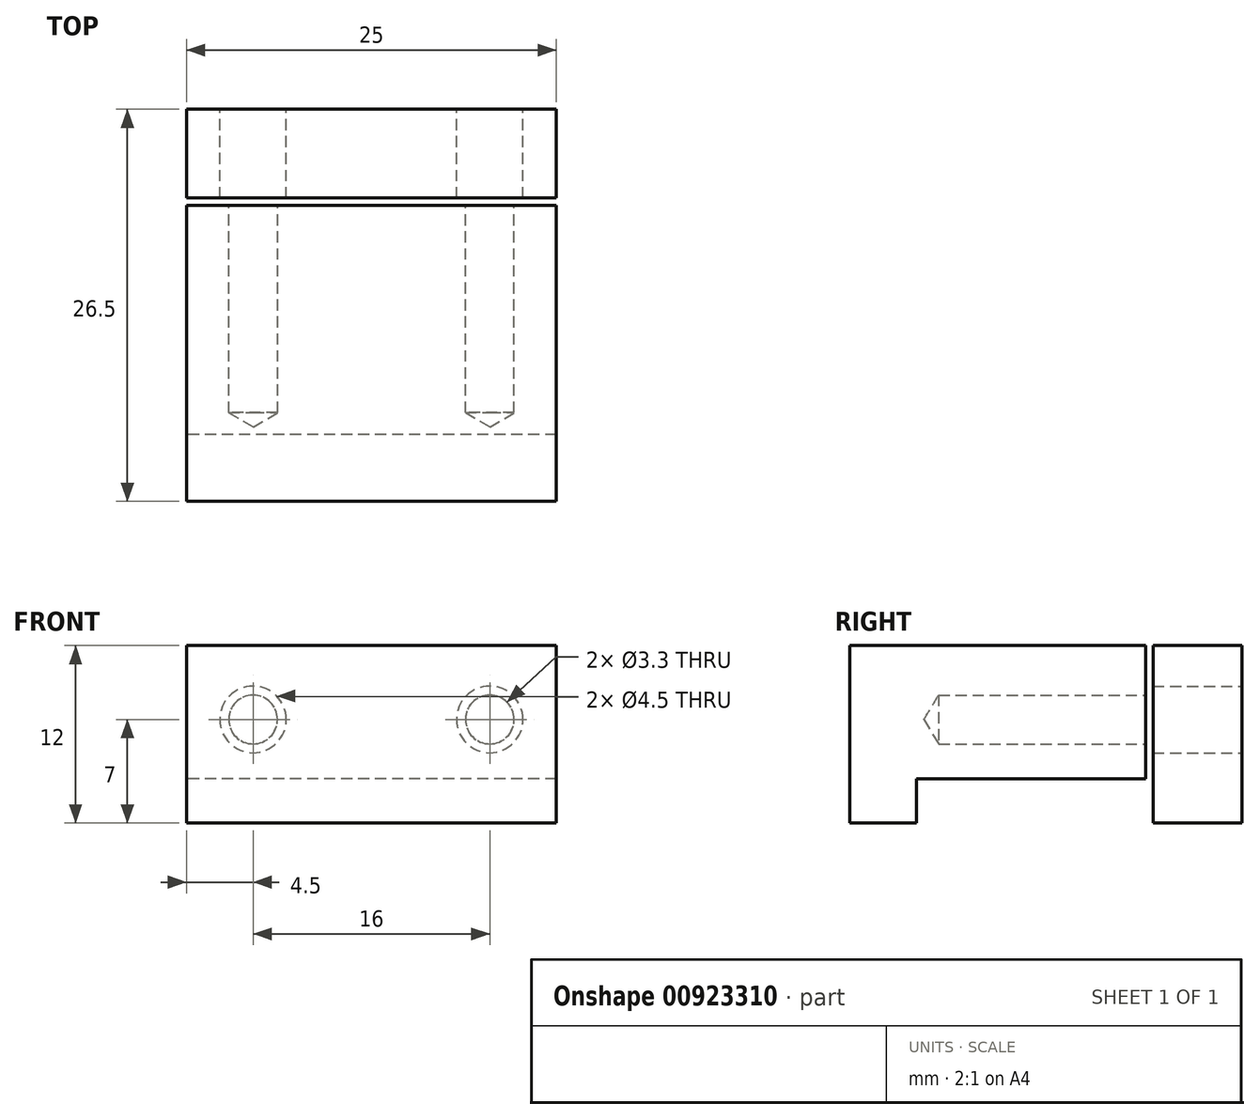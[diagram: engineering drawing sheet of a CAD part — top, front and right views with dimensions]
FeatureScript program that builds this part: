
annotation { "Feature Type Name" : "Feature", "Feature Type Description" : "" }
export const myFeature = defineFeature(function(context is Context, id is Id, definition is map)
    precondition{}
    {
        {
            var Q0;
            Q0=qCreatedBy(makeId("Front.planeOp"),FACE);
            var sketch = newSketch(context, id + "F0", { "sketchPlane" : qUnion([Q0])});
            skLineSegment(sketch, "E0.bottom", {"start": v(12.5, 6) * mm, "end": v(-12.5, 6) * mm});
            skLineSegment(sketch, "E0.top", {"start": v(12.5, -6) * mm, "end": v(-12.5, -6) * mm});
            skLineSegment(sketch, "E0.left", {"start": v(12.5, 6) * mm, "end": v(12.5, -6) * mm});
            skLineSegment(sketch, "E0.right", {"start": v(-12.5, 6) * mm, "end": v(-12.5, -6) * mm});
            skPoint(sketch, "E0.middle", {"position": v(0, 0) * mm});
            skSolve(sketch);
        }
        {
            var Q0;
            Q0 = qSketchRegion(id + "F0", true);
            extrude(context, id + "F1", {"entities" : qUnion([Q0]), "depth" : 20 * mm, "offsetDistance" : 25 * mm});
        }
        {
            var Q0;
            Q0=makeQuery(id+"F1.opExtrude","CAP_FACE",FACE,{"disambiguationData":[OSD([sQuery(id+"F0.wireOp",EDGE,"E0.bottom"),sQuery(id+"F0.wireOp",EDGE,"E0.top"),sQuery(id+"F0.wireOp",EDGE,"E0.left"),sQuery(id+"F0.wireOp",EDGE,"E0.right")])],"isStart":true});
            var sketch = newSketch(context, id + "F2", { "sketchPlane" : qUnion([Q0])});
            skLineSegment(sketch, "E1.bottom", {"start": v(-12.5, -6) * mm, "end": v(12.5, -6) * mm});
            skLineSegment(sketch, "E1.top", {"start": v(-12.5, -3) * mm, "end": v(12.5, -3) * mm});
            skLineSegment(sketch, "E1.left", {"start": v(-12.5, -6) * mm, "end": v(-12.5, -3) * mm});
            skLineSegment(sketch, "E1.right", {"start": v(12.5, -6) * mm, "end": v(12.5, -3) * mm});
            skSolve(sketch);
        }
        {
            var Q0;
            Q0 = qSketchRegion(id + "F2", true);
            extrude(context, id + "F3", {"entities" : qUnion([Q0]), "operationType" : NewBodyOperationType.REMOVE, "oppositeDirection" : true, "depth" : 15.5 * mm, "offsetDistance" : 25 * mm});
        }
        {
            var Q0;
            Q0=makeQuery(id+"F1.opExtrude","CAP_FACE",FACE,{"disambiguationData":[OSD([sQuery(id+"F0.wireOp",EDGE,"E0.bottom"),sQuery(id+"F0.wireOp",EDGE,"E0.top"),sQuery(id+"F0.wireOp",EDGE,"E0.left"),sQuery(id+"F0.wireOp",EDGE,"E0.right")])],"isStart":true});
            cPlane(context, id + "F4", {"entities" : qUnion([Q0]), "cplaneType" : CPlaneType.OFFSET, "offset" : .5 * mm, "width" : 150 * mm, "height" : 150 * mm});
        }
        {
            var Q0;
            Q0=qCreatedBy(id+"F4.planeOp",FACE);
            var sketch = newSketch(context, id + "F5", { "sketchPlane" : qUnion([Q0])});
            skLineSegment(sketch, "E2.bottom", {"start": v(-12.5, 6) * mm, "end": v(12.5, 6) * mm});
            skLineSegment(sketch, "E2.top", {"start": v(-12.5, -6) * mm, "end": v(12.5, -6) * mm});
            skLineSegment(sketch, "E2.left", {"start": v(-12.5, 6) * mm, "end": v(-12.5, -6) * mm});
            skLineSegment(sketch, "E2.right", {"start": v(12.5, 6) * mm, "end": v(12.5, -6) * mm});
            skSolve(sketch);
        }
        {
            var Q0;
            Q0 = qSketchRegion(id + "F5", true);
            extrude(context, id + "F6", {"entities" : qUnion([Q0]), "depth" : 6 * mm, "offsetDistance" : 25 * mm});
        }
        {
            var Q0;
            Q0=makeQuery(id+"F6.opExtrude","CAP_FACE",FACE,{"disambiguationData":[OSD([sQuery(id+"F5.wireOp",EDGE,"E2.bottom"),sQuery(id+"F5.wireOp",EDGE,"E2.top"),sQuery(id+"F5.wireOp",EDGE,"E2.left"),sQuery(id+"F5.wireOp",EDGE,"E2.right")])],"isStart":false});
            var sketch = newSketch(context, id + "F7", { "sketchPlane" : qUnion([Q0])});
            skLineSegment(sketch, "E3", {"start": v(0, 6) * mm, "end": v(0, -6) * mm, "construction": true});
            skPoint(sketch, "E4", {"position": v(-8, 1) * mm});
            skPoint(sketch, "E5.MirrorP", {"position": v(8, 1) * mm});
            skSolve(sketch);
        }
        {
            var Q0;
            Q0=sQuery(id+"F7.wireOp",VERTEX,"E4");
            var Q1;
            Q1=sQuery(id+"F7.wireOp",VERTEX,"E5.MirrorP");
            var Q2;
            Q2=makeQuery(id+"F1.opExtrude","SWEPT_BODY",BODY,{"disambiguationData":[OSD([sQuery(id+"F0.wireOp",EDGE,"E0.bottom"),sQuery(id+"F0.wireOp",EDGE,"E0.top"),sQuery(id+"F0.wireOp",EDGE,"E0.left"),sQuery(id+"F0.wireOp",EDGE,"E0.right")])]});
            var Q3;
            Q3=makeQuery(id+"F6.opExtrude","SWEPT_BODY",BODY,{"disambiguationData":[OSD([sQuery(id+"F5.wireOp",EDGE,"E2.bottom"),sQuery(id+"F5.wireOp",EDGE,"E2.top"),sQuery(id+"F5.wireOp",EDGE,"E2.left"),sQuery(id+"F5.wireOp",EDGE,"E2.right")])]});
            hole(context, id + "F8", {"style" : HoleStyle.SIMPLE, "endStyle" : HoleEndStyle.BLIND_IN_LAST, "standardTappedOrClearance" : lookupTablePath({ "fit" : "Normal", "standard" : "ISO", "engagement" : "75%", "pitch" : "0.7 mm", "size" : "M4", "type" : "Clearance & tapped" }), "standardBlindInLast" : lookupTablePath({ "fit" : "Normal", "standard" : "ISO", "engagement" : "75%", "pitch" : "0.7 mm", "size" : "M4", "type" : "Clearance & tapped" }), "holeDiameter" : 4.5 * mm, "tapDrillDiameter" : 3.3 * mm, "majorDiameter" : 4 * mm, "showTappedDepth" : true, "holeDepth" : 14 * mm, "tappedDepth" : 11.9 * mm, "tapClearance" : 3, "locations" : qUnion([Q0, Q1]), "scope" : qUnion([Q2, Q3])});
        }
    });
